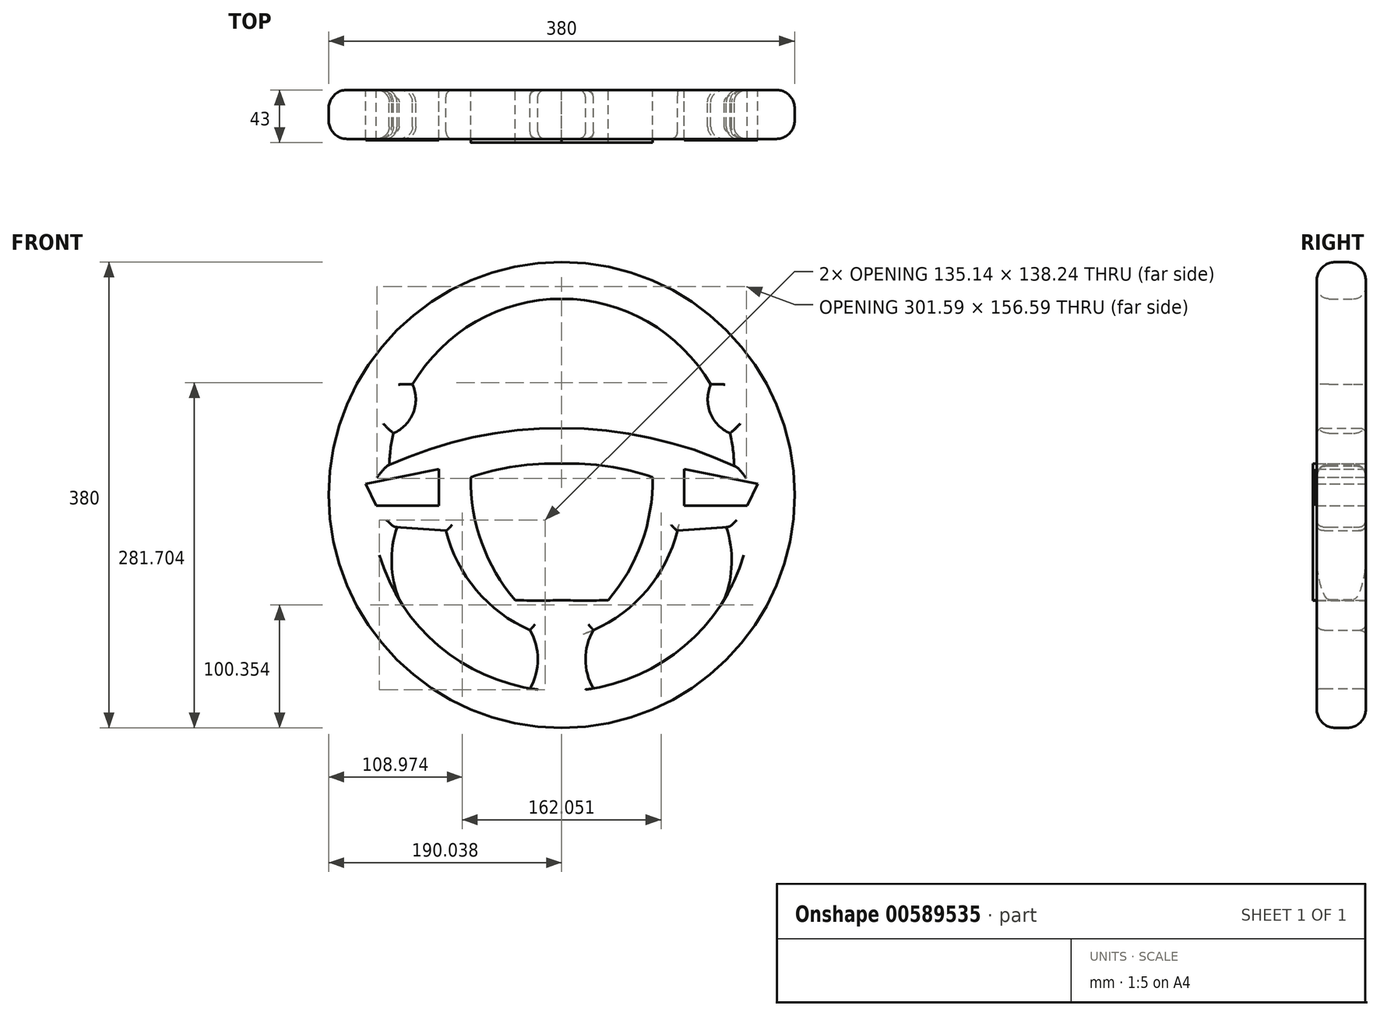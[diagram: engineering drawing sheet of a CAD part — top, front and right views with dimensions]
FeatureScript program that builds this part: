
annotation { "Feature Type Name" : "Feature", "Feature Type Description" : "" }
export const myFeature = defineFeature(function(context is Context, id is Id, definition is map)
    precondition{}
    {
        {
            var Q0;
            Q0=qCreatedBy(makeId("Front.planeOp"),FACE);
            var sketch = newSketch(context, id + "F0", { "sketchPlane" : qUnion([Q0])});
            skCircle(sketch, "E0", {"center": v(0, 0) * mm, "radius": 190 * mm});
            skArc(sketch, "E1", {"start": v(-134.26, -26.17) * mm, "mid": v(-138.65, -55.92) * mm, "end": v(-132.54, -85.37) * mm});
            skLineSegment(sketch, "E2", {"start": v(-134.26, -26.17) * mm, "end": v(-94.37, -29.08) * mm});
            skArc(sketch, "E3", {"start": v(-94.37, -29.08) * mm, "mid": v(-69.6, -77.68) * mm, "end": v(-25.86, -110.3) * mm});
            skArc(sketch, "E4", {"start": v(-25.86, -157.83) * mm, "mid": v(-19.41, -134.06) * mm, "end": v(-25.86, -110.3) * mm});
            skArc(sketch, "E5", {"start": v(140.76, 23.76) * mm, "mid": v(0.12, 54.58) * mm, "end": v(-140.66, 24.43) * mm});
            skPoint(sketch, "E6.endSnap0", {"position": v(0, -170) * mm});
            skArc(sketch, "E7.MirrorCS", {"start": v(132.54, -85.37) * mm, "mid": v(0, -160) * mm, "end": v(-132.54, -85.37) * mm});
            skArc(sketch, "E8", {"start": v(140.76, 23.76) * mm, "mid": v(139.69, 37.14) * mm, "end": v(137.34, 50.36) * mm});
            skArc(sketch, "E9", {"start": v(-137.27, 50.36) * mm, "mid": v(-121.06, 66.97) * mm, "end": v(-121.56, 90.18) * mm});
            skArc(sketch, "E10.trimOffspring", {"start": v(-137.27, 50.36) * mm, "mid": v(-139.57, 37.47) * mm, "end": v(-140.66, 24.43) * mm});
            skArc(sketch, "E11", {"start": v(121.64, 90.18) * mm, "mid": v(121.14, 66.97) * mm, "end": v(137.34, 50.36) * mm});
            skArc(sketch, "E12.trimOffspring", {"start": v(121.64, 90.18) * mm, "mid": v(0.04, 160) * mm, "end": v(-121.56, 90.18) * mm});
            skPoint(sketch, "E13.start.orphan", {"position": v(0, 223.07) * mm});
            skArc(sketch, "E14.MirrorCS", {"start": v(94.37, -29.08) * mm, "mid": v(69.6, -77.68) * mm, "end": v(25.86, -110.3) * mm});
            skArc(sketch, "E15.MirrorCS", {"start": v(25.86, -157.83) * mm, "mid": v(19.41, -134.06) * mm, "end": v(25.86, -110.3) * mm});
            skLineSegment(sketch, "E16.MirrorCS", {"start": v(134.26, -26.17) * mm, "end": v(94.37, -29.08) * mm});
            skArc(sketch, "E17.MirrorCS", {"start": v(134.26, -26.17) * mm, "mid": v(138.65, -55.92) * mm, "end": v(132.54, -85.37) * mm});
            skSolve(sketch);
        }
        {
            var Q0;
            Q0 = qSketchRegion(id + "F0", true);
            extrude(context, id + "F1", {"entities" : qUnion([Q0]), "depth" : 40 * mm, "offsetDistance" : 25 * mm});
        }
        {
            var Q0;
            Q0=qCreatedBy(makeId("Front.planeOp"),FACE);
            var sketch = newSketch(context, id + "F2", { "sketchPlane" : qUnion([Q0])});
            skLineSegment(sketch, "E18", {"start": v(-159.8, 9.2) * mm, "end": v(-151.23, -8.88) * mm});
            skLineSegment(sketch, "E19", {"start": v(-151.23, -8.88) * mm, "end": v(-100, -8.88) * mm});
            skLineSegment(sketch, "E20", {"start": v(-100, -8.88) * mm, "end": v(-100, 21.12) * mm});
            skLineSegment(sketch, "E21", {"start": v(-100, 21.12) * mm, "end": v(-159.8, 9.2) * mm});
            skLineSegment(sketch, "E22", {"start": v(-118.9, 17.35) * mm, "end": v(-113.66, -8.88) * mm});
            skLineSegment(sketch, "E23", {"start": v(-116.27, 4.24) * mm, "end": v(-100, 4.24) * mm});
            skLineSegment(sketch, "E24", {"start": v(-137.2, 13.7) * mm, "end": v(-132.7, -8.88) * mm});
            skLineSegment(sketch, "E25", {"start": v(-155.84, 0.84) * mm, "end": v(-134.64, 0.84) * mm});
            skLineSegment(sketch, "E26", {"start": v(-155.84, 0.16) * mm, "end": v(-134.5, 0.16) * mm});
            skPoint(sketch, "E26.startSnap0", {"position": v(-155.5, 0.16) * mm});
            skLineSegment(sketch, "E27", {"start": v(-116.13, 3.5) * mm, "end": v(-100, 3.5) * mm});
            skLineSegment(sketch, "E28", {"start": v(-119.65, 17.2) * mm, "end": v(-114.45, -8.88) * mm});
            skLineSegment(sketch, "E29", {"start": v(-136.48, 13.84) * mm, "end": v(-131.95, -8.88) * mm});
            skLineSegment(sketch, "E30", {"start": v(0, 155.46) * mm, "end": v(0, -130.11) * mm, "construction": true});
            skLineSegment(sketch, "E31.MirrorCS", {"start": v(116.13, 3.5) * mm, "end": v(100, 3.5) * mm});
            skLineSegment(sketch, "E32.MirrorCS", {"start": v(118.9, 17.35) * mm, "end": v(113.66, -8.88) * mm});
            skLineSegment(sketch, "E33.MirrorCS", {"start": v(151.23, -8.88) * mm, "end": v(100, -8.88) * mm});
            skLineSegment(sketch, "E34.MirrorCS", {"start": v(159.8, 9.2) * mm, "end": v(151.23, -8.88) * mm});
            skLineSegment(sketch, "E35.MirrorCS", {"start": v(155.84, 0.84) * mm, "end": v(134.64, 0.84) * mm});
            skLineSegment(sketch, "E36.MirrorCS", {"start": v(155.84, 0.16) * mm, "end": v(134.5, 0.16) * mm});
            skLineSegment(sketch, "E37.MirrorCS", {"start": v(119.65, 17.2) * mm, "end": v(114.45, -8.88) * mm});
            skLineSegment(sketch, "E38.MirrorCS", {"start": v(136.48, 13.84) * mm, "end": v(131.95, -8.88) * mm});
            skLineSegment(sketch, "E39.MirrorCS", {"start": v(116.27, 4.24) * mm, "end": v(100, 4.24) * mm});
            skPoint(sketch, "E40.MirrorP", {"position": v(155.5, 0.16) * mm});
            skLineSegment(sketch, "E41.MirrorCS", {"start": v(137.2, 13.7) * mm, "end": v(132.7, -8.88) * mm});
            skLineSegment(sketch, "E42.MirrorCS", {"start": v(100, 21.12) * mm, "end": v(159.8, 9.2) * mm});
            skLineSegment(sketch, "E43.MirrorCS", {"start": v(100, -8.88) * mm, "end": v(100, 21.12) * mm});
            skSolve(sketch);
        }
        {
            var Q0;
            Q0 = qSketchRegion(id + "F2", true);
            var Q1;
            Q1 = qConstructionFilter(qBodyType(qCreatedBy(id + "F2" ,EDGE), BodyType.WIRE), ConstructionObject.NO);
            extrude(context, id + "F3", {"entities" : qUnion([Q0]), "surfaceEntities" : qUnion([Q1]), "depth" : 41 * mm, "offsetDistance" : 25 * mm});
        }
        {
            var Q0;
            Q0=makeQuery(id+"F0.imprint","IMPRINT",FACE,{"disambiguationData":[TD([[makeQuery(id+"F0.imprint","IMPRINT",EDGE,{"derivedFrom":sQuery(id+"F0.wireOp",EDGE,"E0")}),1.0]])]});
            extrude(context, id + "F4", {"entities" : qUnion([Q0]), "depth" : 40 * mm, "offsetDistance" : 25 * mm});
        }
        {
            var Q0;
            Q0=qCreatedBy(makeId("Front.planeOp"),FACE);
            var sketch = newSketch(context, id + "F5", { "sketchPlane" : qUnion([Q0])});
            skArc(sketch, "E44", {"start": v(37.85, -85.83) * mm, "mid": v(65.23, -39.02) * mm, "end": v(74.17, 14.46) * mm});
            skArc(sketch, "E45", {"start": v(0, -85.83) * mm, "mid": v(18.93, -86.16) * mm, "end": v(37.85, -85.83) * mm});
            skArc(sketch, "E46", {"start": v(74.17, 14.46) * mm, "mid": v(37.6, 23.48) * mm, "end": v(0, 25.5) * mm});
            skArc(sketch, "E47.MirrorCS", {"start": v(-74.17, 14.46) * mm, "mid": v(-37.6, 23.48) * mm, "end": v(0, 25.5) * mm});
            skArc(sketch, "E48.MirrorCS", {"start": v(-37.85, -85.83) * mm, "mid": v(-65.23, -39.02) * mm, "end": v(-74.17, 14.46) * mm});
            skArc(sketch, "E49.MirrorCS", {"start": v(0, -85.83) * mm, "mid": v(-18.93, -86.16) * mm, "end": v(-37.85, -85.83) * mm});
            skSolve(sketch);
        }
        {
            var Q0;
            Q0 = qSketchRegion(id + "F5", true);
            extrude(context, id + "F6", {"entities" : qUnion([Q0]), "depth" : 43 * mm, "offsetDistance" : 25 * mm});
        }
        {
            var Q0;
            Q0=makeQuery(id+"F4.opExtrude","CAP_EDGE",EDGE,{"disambiguationData":[OSD([sQuery(id+"F0.wireOp",EDGE,"E12.trimOffspring")])],"isStart":true});
            var Q1;
            {var subQ0=sQuery(id+"F0.wireOp",EDGE,"E7.MirrorCS");Q1=makeQuery(id+"F4.opExtrude","CAP_EDGE",EDGE,{"disambiguationData":[OSD([subQ0]),TDD([makeQuery(id+"F0.imprint","IMPRINT",EDGE,{"disambiguationData":[TD([[makeQuery(id+"F0.imprint","INTERSECT",VERTEX,{"derivedFrom":[sQuery(id+"F0.wireOp",EDGE,"E1"),subQ0]}),1.0]])],"derivedFrom":subQ0})])],"isStart":false});}
            var Q2;
            {var subQ0=sQuery(id+"F0.wireOp",EDGE,"E7.MirrorCS");Q2=makeQuery(id+"F4.opExtrude","CAP_EDGE",EDGE,{"disambiguationData":[OSD([subQ0]),TDD([makeQuery(id+"F0.imprint","IMPRINT",EDGE,{"disambiguationData":[TD([[makeQuery(id+"F0.imprint","INTERSECT",VERTEX,{"derivedFrom":[subQ0,sQuery(id+"F0.wireOp",EDGE,"E17.MirrorCS")]}),-1.0]])],"derivedFrom":subQ0})])],"isStart":false});}
            var Q3;
            Q3=makeQuery(id+"F4.opExtrude","CAP_EDGE",EDGE,{"disambiguationData":[OSD([sQuery(id+"F0.wireOp",EDGE,"E17.MirrorCS")])],"isStart":true});
            var Q4;
            Q4=makeQuery(id+"F4.opExtrude","CAP_EDGE",EDGE,{"disambiguationData":[OSD([sQuery(id+"F0.wireOp",EDGE,"E17.MirrorCS")])],"isStart":false});
            var Q5;
            Q5=makeQuery(id+"F4.opExtrude","CAP_EDGE",EDGE,{"disambiguationData":[OSD([sQuery(id+"F0.wireOp",EDGE,"E1")])],"isStart":true});
            var Q6;
            Q6=makeQuery(id+"F4.opExtrude","CAP_EDGE",EDGE,{"disambiguationData":[OSD([sQuery(id+"F0.wireOp",EDGE,"E1")])],"isStart":false});
            var Q7;
            {var subQ0=sQuery(id+"F0.wireOp",EDGE,"E7.MirrorCS");Q7=makeQuery(id+"F4.opExtrude","CAP_EDGE",EDGE,{"disambiguationData":[OSD([subQ0]),TDD([makeQuery(id+"F0.imprint","IMPRINT",EDGE,{"disambiguationData":[TD([[makeQuery(id+"F0.imprint","INTERSECT",VERTEX,{"derivedFrom":[sQuery(id+"F0.wireOp",EDGE,"E1"),subQ0]}),1.0]])],"derivedFrom":subQ0})])],"isStart":true});}
            var Q8;
            {var subQ0=sQuery(id+"F0.wireOp",EDGE,"E7.MirrorCS");Q8=makeQuery(id+"F4.opExtrude","CAP_EDGE",EDGE,{"disambiguationData":[OSD([subQ0]),TDD([makeQuery(id+"F0.imprint","IMPRINT",EDGE,{"disambiguationData":[TD([[makeQuery(id+"F0.imprint","INTERSECT",VERTEX,{"derivedFrom":[subQ0,sQuery(id+"F0.wireOp",EDGE,"E17.MirrorCS")]}),-1.0]])],"derivedFrom":subQ0})])],"isStart":true});}
            var Q9;
            Q9=makeQuery(id+"F4.opExtrude","CAP_EDGE",EDGE,{"disambiguationData":[OSD([sQuery(id+"F0.wireOp",EDGE,"E12.trimOffspring")])],"isStart":false});
            var Q10;
            Q10=makeQuery(id+"F4.opExtrude","CAP_EDGE",EDGE,{"disambiguationData":[OSD([sQuery(id+"F0.wireOp",EDGE,"E9")])],"isStart":false});
            var Q11;
            Q11=makeQuery(id+"F4.opExtrude","CAP_EDGE",EDGE,{"disambiguationData":[OSD([sQuery(id+"F0.wireOp",EDGE,"E9")])],"isStart":true});
            var Q12;
            Q12=makeQuery(id+"F4.opExtrude","CAP_EDGE",EDGE,{"disambiguationData":[OSD([sQuery(id+"F0.wireOp",EDGE,"E10.trimOffspring")])],"isStart":false});
            var Q13;
            Q13=makeQuery(id+"F4.opExtrude","CAP_EDGE",EDGE,{"disambiguationData":[OSD([sQuery(id+"F0.wireOp",EDGE,"E10.trimOffspring")])],"isStart":true});
            var Q14;
            Q14=makeQuery(id+"F4.opExtrude","CAP_EDGE",EDGE,{"disambiguationData":[OSD([sQuery(id+"F0.wireOp",EDGE,"E11")])],"isStart":true});
            var Q15;
            Q15=makeQuery(id+"F4.opExtrude","CAP_EDGE",EDGE,{"disambiguationData":[OSD([sQuery(id+"F0.wireOp",EDGE,"E11")])],"isStart":false});
            var Q16;
            Q16=makeQuery(id+"F4.opExtrude","CAP_EDGE",EDGE,{"disambiguationData":[OSD([sQuery(id+"F0.wireOp",EDGE,"E8")])],"isStart":false});
            var Q17;
            Q17=makeQuery(id+"F4.opExtrude","CAP_EDGE",EDGE,{"disambiguationData":[OSD([sQuery(id+"F0.wireOp",EDGE,"E8")])],"isStart":true});
            fillet(context, id + "F7", {"entities" : qUnion([Q0, Q1, Q2, Q3, Q4, Q5, Q6, Q7, Q8, Q9, Q10, Q11, Q12, Q13, Q14, Q15, Q16, Q17]), "radius" : 10 * mm, "tangentPropagation" : true, "allowEdgeOverflow" : false});
        }
        {
            var Q0;
            Q0=makeQuery(id+"F1.opExtrude","SWEPT_BODY",BODY,{"disambiguationData":[OSD([sQuery(id+"F0.wireOp",EDGE,"E0"),sQuery(id+"F0.wireOp",EDGE,"E1"),sQuery(id+"F0.wireOp",EDGE,"E2"),sQuery(id+"F0.wireOp",EDGE,"E3"),sQuery(id+"F0.wireOp",EDGE,"E4"),sQuery(id+"F0.wireOp",EDGE,"E5"),sQuery(id+"F0.wireOp",EDGE,"E7.MirrorCS"),sQuery(id+"F0.wireOp",EDGE,"E8"),sQuery(id+"F0.wireOp",EDGE,"E9"),sQuery(id+"F0.wireOp",EDGE,"E10.trimOffspring"),sQuery(id+"F0.wireOp",EDGE,"E11"),sQuery(id+"F0.wireOp",EDGE,"E12.trimOffspring"),sQuery(id+"F0.wireOp",EDGE,"E14.MirrorCS"),sQuery(id+"F0.wireOp",EDGE,"E15.MirrorCS"),sQuery(id+"F0.wireOp",EDGE,"E16.MirrorCS"),sQuery(id+"F0.wireOp",EDGE,"E17.MirrorCS")])]});
            deleteBodies(context, id + "F8", {"entities" : qUnion([Q0])});
        }
        {
            var Q0;
            Q0=makeQuery(id+"F4.opExtrude","CAP_EDGE",EDGE,{"disambiguationData":[OSD([sQuery(id+"F0.wireOp",EDGE,"E0")])],"isStart":false});
            var Q1;
            Q1=makeQuery(id+"F4.opExtrude","CAP_EDGE",EDGE,{"disambiguationData":[OSD([sQuery(id+"F0.wireOp",EDGE,"E0")])],"isStart":true});
            fillet(context, id + "F9", {"entities" : qUnion([Q0, Q1]), "radius" : 15 * mm, "tangentPropagation" : true, "allowEdgeOverflow" : false});
        }
        {
            var Q0;
            Q0=makeQuery(id+"F4.opExtrude","CAP_EDGE",EDGE,{"disambiguationData":[OSD([sQuery(id+"F0.wireOp",EDGE,"E3")])],"isStart":false});
            var Q1;
            Q1=makeQuery(id+"F4.opExtrude","CAP_EDGE",EDGE,{"disambiguationData":[OSD([sQuery(id+"F0.wireOp",EDGE,"E4")])],"isStart":false});
            var Q2;
            Q2=makeQuery(id+"F4.opExtrude","CAP_EDGE",EDGE,{"disambiguationData":[OSD([sQuery(id+"F0.wireOp",EDGE,"E14.MirrorCS")])],"isStart":false});
            var Q3;
            Q3=makeQuery(id+"F4.opExtrude","CAP_EDGE",EDGE,{"disambiguationData":[OSD([sQuery(id+"F0.wireOp",EDGE,"E15.MirrorCS")])],"isStart":false});
            var Q4;
            Q4=makeQuery(id+"F4.opExtrude","CAP_EDGE",EDGE,{"disambiguationData":[OSD([sQuery(id+"F0.wireOp",EDGE,"E3")])],"isStart":true});
            var Q5;
            Q5=makeQuery(id+"F4.opExtrude","CAP_EDGE",EDGE,{"disambiguationData":[OSD([sQuery(id+"F0.wireOp",EDGE,"E4")])],"isStart":true});
            var Q6;
            Q6=makeQuery(id+"F4.opExtrude","CAP_EDGE",EDGE,{"disambiguationData":[OSD([sQuery(id+"F0.wireOp",EDGE,"E15.MirrorCS")])],"isStart":true});
            fillet(context, id + "F10", {"entities" : qUnion([Q0, Q1, Q2, Q3, Q4, Q5, Q6]), "radius" : 6 * mm, "tangentPropagation" : true, "allowEdgeOverflow" : false});
        }
        {
            var Q0;
            Q0=makeQuery(id+"F4.opExtrude","CAP_EDGE",EDGE,{"disambiguationData":[OSD([sQuery(id+"F0.wireOp",EDGE,"E5")])],"isStart":false});
            var Q1;
            Q1=makeQuery(id+"F4.opExtrude","CAP_EDGE",EDGE,{"disambiguationData":[OSD([sQuery(id+"F0.wireOp",EDGE,"E5")])],"isStart":true});
            var Q2;
            Q2=makeQuery(id+"F4.opExtrude","CAP_EDGE",EDGE,{"disambiguationData":[OSD([sQuery(id+"F0.wireOp",EDGE,"E2")])],"isStart":false});
            var Q3;
            Q3=makeQuery(id+"F4.opExtrude","CAP_EDGE",EDGE,{"disambiguationData":[OSD([sQuery(id+"F0.wireOp",EDGE,"E16.MirrorCS")])],"isStart":false});
            var Q4;
            Q4=makeQuery(id+"F4.opExtrude","CAP_EDGE",EDGE,{"disambiguationData":[OSD([sQuery(id+"F0.wireOp",EDGE,"E2")])],"isStart":true});
            var Q5;
            Q5=makeQuery(id+"F4.opExtrude","CAP_EDGE",EDGE,{"disambiguationData":[OSD([sQuery(id+"F0.wireOp",EDGE,"E16.MirrorCS")])],"isStart":true});
            fillet(context, id + "F11", {"entities" : qUnion([Q0, Q1, Q2, Q3, Q4, Q5]), "radius" : 5 * mm, "tangentPropagation" : true, "allowEdgeOverflow" : false});
        }
    });
